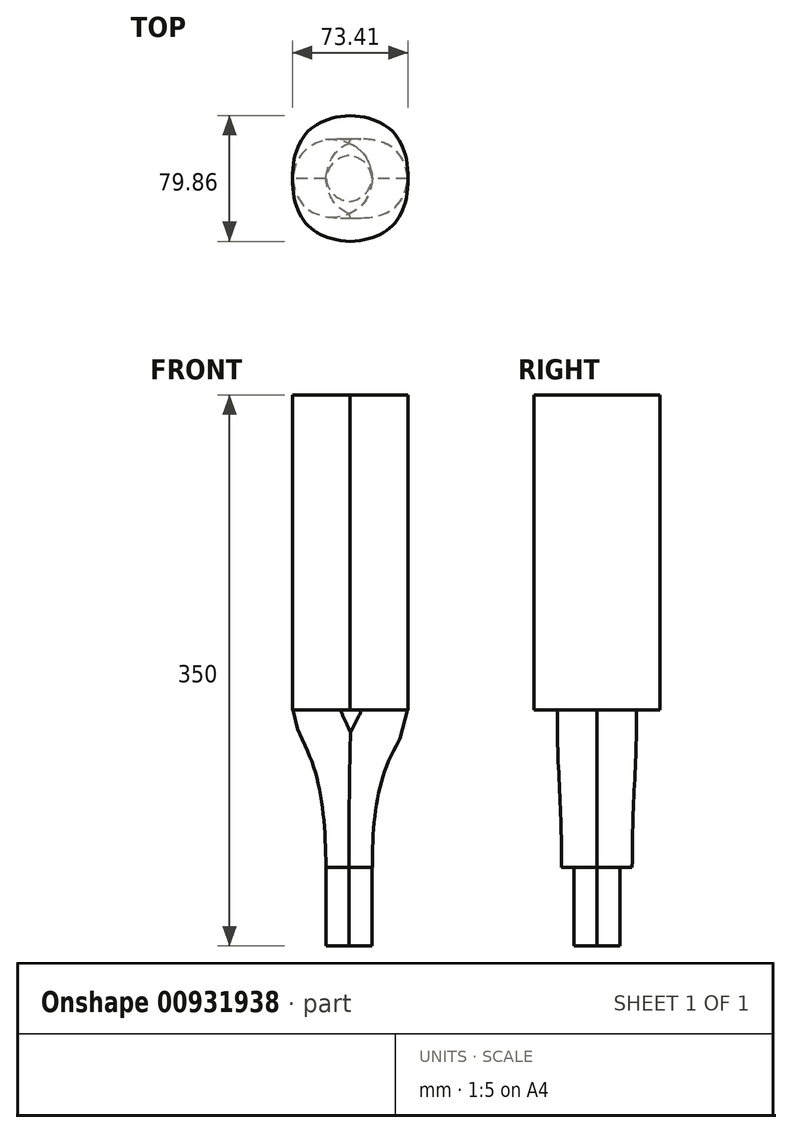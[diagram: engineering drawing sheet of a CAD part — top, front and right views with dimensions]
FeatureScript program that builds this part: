
annotation { "Feature Type Name" : "Feature", "Feature Type Description" : "" }
export const myFeature = defineFeature(function(context is Context, id is Id, definition is map)
    precondition{}
    {
        {
            var Q0;
            Q0=qCreatedBy(makeId("Front.planeOp"),FACE);
            var sketch = newSketch(context, id + "F0", { "sketchPlane" : qUnion([Q0])});
            skLineSegment(sketch, "E0.bottom", {"start": v(-17.96, -125.57) * mm, "end": v(12.04, -125.57) * mm});
            skLineSegment(sketch, "E0.top", {"start": v(-17.96, -75.57) * mm, "end": v(12.04, -75.57) * mm});
            skLineSegment(sketch, "E0.left", {"start": v(-17.96, -125.57) * mm, "end": v(-17.96, -75.57) * mm});
            skLineSegment(sketch, "E0.right", {"start": v(12.04, -125.57) * mm, "end": v(12.04, -75.57) * mm});
            skLineSegment(sketch, "E1.bottom", {"start": v(-38.93, 224.43) * mm, "end": v(34.48, 224.43) * mm});
            skLineSegment(sketch, "E1.top", {"start": v(-38.93, 24.43) * mm, "end": v(34.48, 24.43) * mm});
            skLineSegment(sketch, "E1.left", {"start": v(-38.93, 224.43) * mm, "end": v(-38.93, 24.43) * mm});
            skLineSegment(sketch, "E1.right", {"start": v(34.48, 224.43) * mm, "end": v(34.48, 24.43) * mm});
            skFitSpline(sketch, "E2", {"points": [v(-38.93, 24.43) * mm, v(-17.96, -75.57) * mm], "startDerivative": vector(7.24, -73.28) * mm, "endDerivative": vector(1.34, -226.72) * mm});
            skFitSpline(sketch, "E3", {"points": [v(12.04, -75.57) * mm, v(34.48, 24.43) * mm], "startDerivative": vector(-1, 226.72) * mm, "endDerivative": vector(-1, 73.28) * mm});
            skSolve(sketch);
        }
        {
            var Q0;
            Q0=makeQuery(id+"F0.imprint","IMPRINT",FACE,{"disambiguationData":[TD([[makeQuery(id+"F0.imprint","IMPRINT",EDGE,{"derivedFrom":sQuery(id+"F0.wireOp",EDGE,"E1.bottom")}),-1.0]])]});
            extrude(context, id + "F1", {"entities" : qUnion([Q0]), "endBound" : BoundingType.SYMMETRIC, "depth" : 80 * mm, "offsetDistance" : 25 * mm});
        }
        {
            var Q0;
            Q0=makeQuery(id+"F0.imprint","IMPRINT",FACE,{"disambiguationData":[TD([[makeQuery(id+"F0.imprint","IMPRINT",EDGE,{"derivedFrom":sQuery(id+"F0.wireOp",EDGE,"E0.bottom")}),1.0]])]});
            extrude(context, id + "F2", {"entities" : qUnion([Q0]), "endBound" : BoundingType.SYMMETRIC, "depth" : 30 * mm, "offsetDistance" : 25 * mm});
        }
        {
            var Q0;
            Q0=makeQuery(id+"F0.imprint","IMPRINT",FACE,{"disambiguationData":[TD([[makeQuery(id+"F0.imprint","IMPRINT",EDGE,{"derivedFrom":sQuery(id+"F0.wireOp",EDGE,"E0.top")}),1.0]])]});
            extrude(context, id + "F3", {"entities" : qUnion([Q0]), "endBound" : BoundingType.SYMMETRIC, "depth" : 50 * mm, "offsetDistance" : 25 * mm});
        }
        {
            var Q0;
            Q0=makeQuery(id+"F1.opExtrude","CAP_EDGE",EDGE,{"disambiguationData":[OSD([sQuery(id+"F0.wireOp",EDGE,"E1.left")])],"isStart":true});
            var Q1;
            Q1=makeQuery(id+"F1.opExtrude","CAP_EDGE",EDGE,{"disambiguationData":[OSD([sQuery(id+"F0.wireOp",EDGE,"E1.right")])],"isStart":true});
            var Q2;
            Q2=makeQuery(id+"F1.opExtrude","CAP_EDGE",EDGE,{"disambiguationData":[OSD([sQuery(id+"F0.wireOp",EDGE,"E1.right")])],"isStart":false});
            var Q3;
            Q3=makeQuery(id+"F1.opExtrude","CAP_EDGE",EDGE,{"disambiguationData":[OSD([sQuery(id+"F0.wireOp",EDGE,"E1.left")])],"isStart":false});
            fillet(context, id + "F4", {"entities" : qUnion([Q0, Q1, Q2, Q3]), "radius" : 40 * mm, "tangentPropagation" : true, "rho" : 0.5, "crossSection" : FilletCrossSection.CONIC, "allowEdgeOverflow" : false});
        }
        {
            var Q0;
            Q0=makeQuery(id+"F2.opExtrude","CAP_EDGE",EDGE,{"disambiguationData":[OSD([sQuery(id+"F0.wireOp",EDGE,"E0.left")])],"isStart":true});
            var Q1;
            Q1=makeQuery(id+"F2.opExtrude","CAP_EDGE",EDGE,{"disambiguationData":[OSD([sQuery(id+"F0.wireOp",EDGE,"E0.left")])],"isStart":false});
            var Q2;
            Q2=makeQuery(id+"F2.opExtrude","CAP_EDGE",EDGE,{"disambiguationData":[OSD([sQuery(id+"F0.wireOp",EDGE,"E0.right")])],"isStart":true});
            var Q3;
            Q3=makeQuery(id+"F2.opExtrude","CAP_EDGE",EDGE,{"disambiguationData":[OSD([sQuery(id+"F0.wireOp",EDGE,"E0.right")])],"isStart":false});
            fillet(context, id + "F5", {"entities" : qUnion([Q0, Q1, Q2, Q3]), "radius" : 20 * mm, "tangentPropagation" : true, "rho" : 0.5, "crossSection" : FilletCrossSection.CONIC, "allowEdgeOverflow" : false});
        }
        {
            var Q0;
            Q0=makeQuery(id+"F3.opExtrude","CAP_EDGE",EDGE,{"disambiguationData":[OSD([sQuery(id+"F0.wireOp",EDGE,"E3")])],"isStart":true});
            var Q1;
            Q1=makeQuery(id+"F3.opExtrude","CAP_EDGE",EDGE,{"disambiguationData":[OSD([sQuery(id+"F0.wireOp",EDGE,"E3")])],"isStart":false});
            var Q2;
            Q2=makeQuery(id+"F3.opExtrude","CAP_EDGE",EDGE,{"disambiguationData":[OSD([sQuery(id+"F0.wireOp",EDGE,"E2")])],"isStart":false});
            var Q3;
            Q3=makeQuery(id+"F3.opExtrude","CAP_EDGE",EDGE,{"disambiguationData":[OSD([sQuery(id+"F0.wireOp",EDGE,"E2")])],"isStart":true});
            fillet(context, id + "F6", {"entities" : qUnion([Q0, Q1, Q2, Q3]), "radius" : 30 * mm, "tangentPropagation" : true, "rho" : 0.5, "crossSection" : FilletCrossSection.CONIC, "allowEdgeOverflow" : false});
        }
    });
